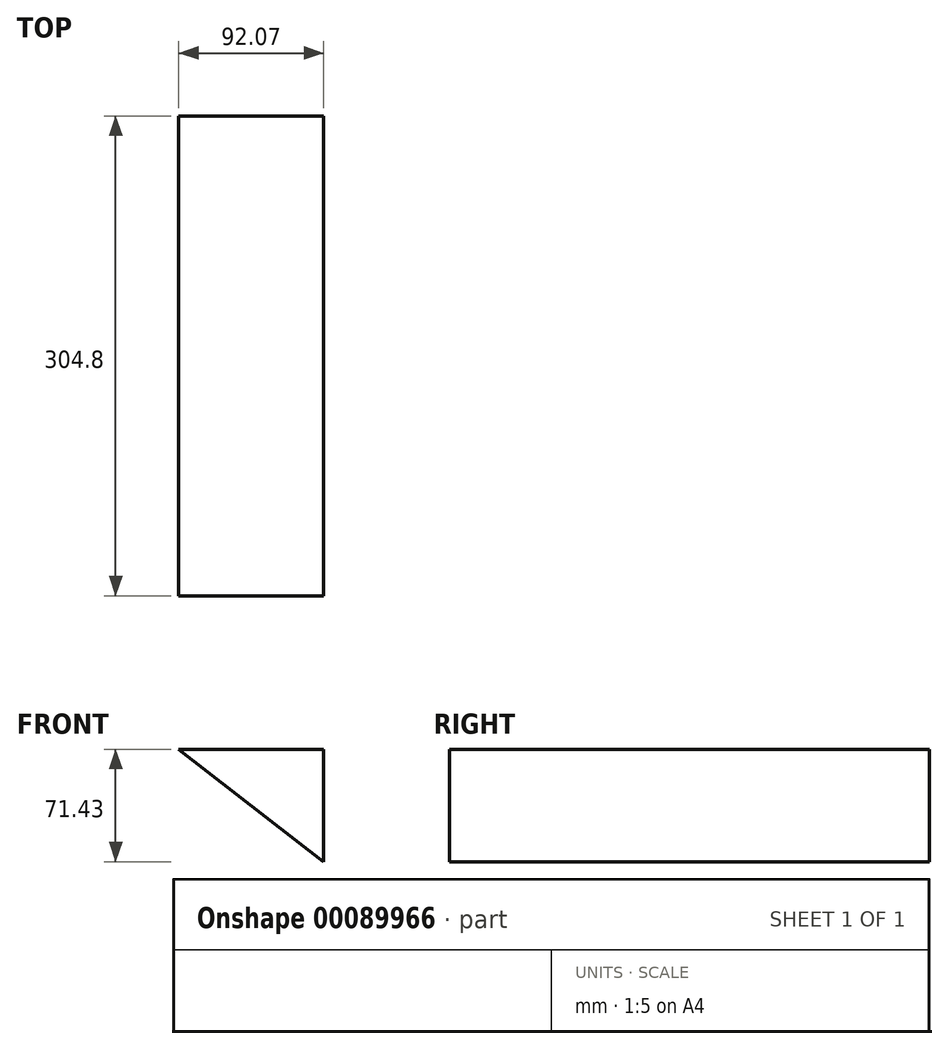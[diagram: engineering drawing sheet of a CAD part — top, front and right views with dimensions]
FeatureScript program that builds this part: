
annotation { "Feature Type Name" : "Feature", "Feature Type Description" : "" }
export const myFeature = defineFeature(function(context is Context, id is Id, definition is map)
    precondition{}
    {
        {
            var Q0;
            Q0=qCreatedBy(makeId("Front.planeOp"),FACE);
            var sketch = newSketch(context, id + "F0", { "sketchPlane" : qUnion([Q0])});
            skLineSegment(sketch, "E0", {"start": v(-114.09, 36.62) * mm, "end": v(-22.02, 36.62) * mm});
            skLineSegment(sketch, "E1", {"start": v(-22.02, 36.62) * mm, "end": v(-22.02, -34.81) * mm});
            skLineSegment(sketch, "E2", {"start": v(-22.02, -34.81) * mm, "end": v(-114.09, 36.62) * mm});
            skSolve(sketch);
        }
        {
            var Q0;
            Q0 = qSketchRegion(id + "F0", true);
            extrude(context, id + "F1", {"entities" : qUnion([Q0]), "endBound" : BoundingType.SYMMETRIC, "oppositeDirection" : true, "depth" : 304.8 * mm});
        }
    });
